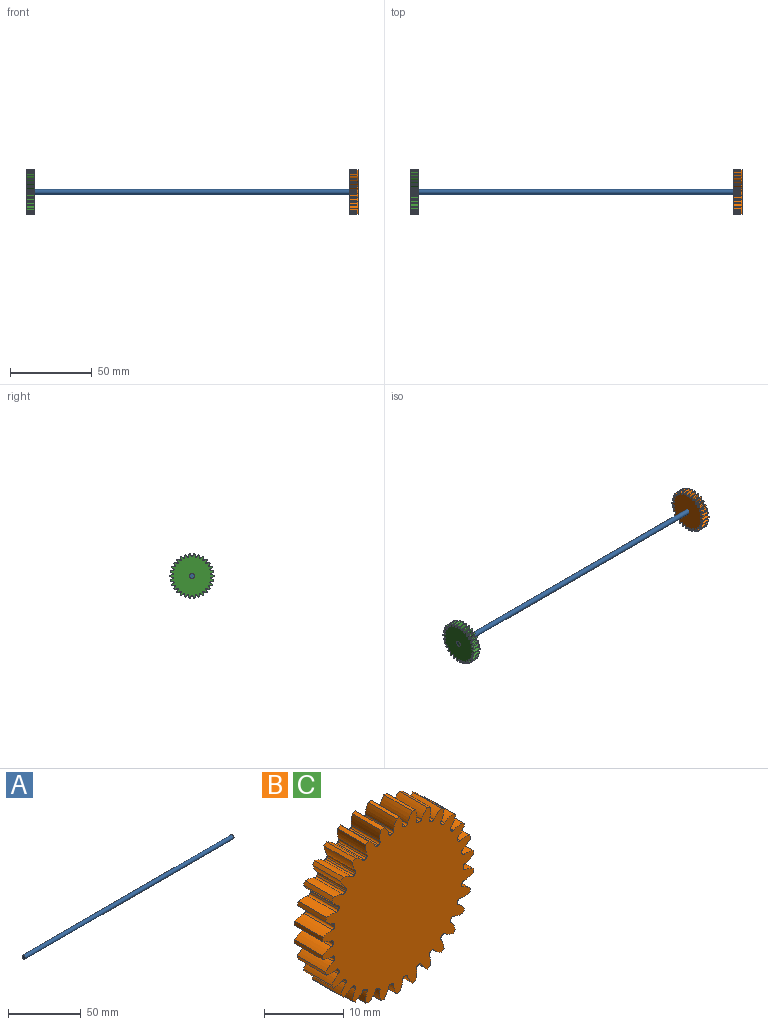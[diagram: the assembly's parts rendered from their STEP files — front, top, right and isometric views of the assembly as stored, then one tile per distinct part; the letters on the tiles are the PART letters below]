
ASSEMBLY  parts=3 mates=2
PART A: 3 faces, bbox 203.2x3.2x3.2 mm
  f0: cylinder r=1.59mm len=203.2mm, axis (-1,0,0), area 2026.8mm2, adj f1,f2
  f1: plane 3.18x3.18mm, normal (1,0,0), area 7.9mm2, adj f0
  f2: plane 3.18x3.18mm, normal (-1,0,0), area 7.9mm2, adj f0
PART B: 182 faces, bbox 27x5.1x27.1 mm
  f0: cylinder r=13.55mm len=5.08mm, axis (0,1,0), area 3.2mm2, adj f29,f31,f172,f179
  f1: cylinder r=13.55mm len=5.08mm, axis (0,1,0), area 3.2mm2, adj f29,f31,f167,f174
  f2: cylinder r=13.55mm len=5.08mm, axis (0,1,0), area 3.2mm2, adj f29,f31,f162,f169
  f3: cylinder r=13.55mm len=5.08mm, axis (0,1,0), area 3.2mm2, adj f29,f31,f152,f164
  f4: cylinder r=13.55mm len=5.08mm, axis (0,1,0), area 3.2mm2, adj f29,f31,f147,f159
  f5: cylinder r=13.55mm len=5.08mm, axis (0,1,0), area 3.2mm2, adj f29,f31,f154,f157
  f6: cylinder r=13.55mm len=5.08mm, axis (0,1,0), area 3.2mm2, adj f29,f31,f142,f149
  f7: cylinder r=13.55mm len=5.08mm, axis (0,1,0), area 3.2mm2, adj f29,f31,f32,f144
  f8: cylinder r=13.55mm len=5.08mm, axis (0,1,0), area 3.2mm2, adj f29,f31,f127,f139
  f9: cylinder r=13.55mm len=5.08mm, axis (0,1,0), area 3.2mm2, adj f29,f31,f134,f137
  f10: cylinder r=13.55mm len=5.08mm, axis (0,1,0), area 3.2mm2, adj f29,f31,f122,f129
  f11: cylinder r=13.55mm len=5.08mm, axis (0,1,0), area 3.2mm2, adj f29,f31,f124,f177
  f12: cylinder r=13.55mm len=5.08mm, axis (0,1,0), area 3.2mm2, adj f29,f31,f119,f132
  f13: cylinder r=13.55mm len=5.08mm, axis (0,1,0), area 3.2mm2, adj f29,f31,f114,f117
  f14: cylinder r=13.55mm len=5.08mm, axis (0,1,0), area 3.2mm2, adj f29,f31,f109,f112
  f15: cylinder r=13.55mm len=5.08mm, axis (0,1,0), area 3.2mm2, adj f29,f31,f104,f107
  f16: cylinder r=13.55mm len=5.08mm, axis (0,1,0), area 3.2mm2, adj f29,f31,f87,f99
  f17: cylinder r=13.55mm len=5.08mm, axis (0,1,0), area 3.2mm2, adj f29,f31,f94,f97
  f18: cylinder r=13.55mm len=5.08mm, axis (0,1,0), area 3.2mm2, adj f29,f31,f82,f89
  f19: cylinder r=13.55mm len=5.08mm, axis (0,1,0), area 3.2mm2, adj f29,f31,f84,f102
  f20: cylinder r=13.55mm len=5.08mm, axis (0,1,0), area 3.2mm2, adj f29,f31,f79,f92
  f21: cylinder r=13.55mm len=5.08mm, axis (0,1,0), area 3.2mm2, adj f29,f31,f74,f77
  f22: cylinder r=13.55mm len=5.08mm, axis (0,1,0), area 3.2mm2, adj f29,f31,f69,f72
  f23: cylinder r=13.55mm len=5.08mm, axis (0,1,0), area 3.2mm2, adj f29,f31,f64,f67
  f24: cylinder r=13.55mm len=5.08mm, axis (0,1,0), area 3.2mm2, adj f29,f31,f52,f59
  f25: cylinder r=13.55mm len=5.08mm, axis (0,1,0), area 3.2mm2, adj f29,f31,f42,f54
  f26: cylinder r=13.55mm len=5.08mm, axis (0,1,0), area 3.2mm2, adj f29,f31,f49,f62
  f27: cylinder r=13.55mm len=5.08mm, axis (0,1,0), area 3.2mm2, adj f29,f31,f44,f47
  f28: cylinder r=13.55mm len=5.08mm, axis (0,1,0), area 3.2mm2, adj f29,f31,f39,f57
  f29: plane 27.09x27.01mm, normal (0,-1,0), area 501mm2, adj f0,f1,f2,f3,f4,f5,f6,f7
  f30: cylinder r=13.55mm len=5.08mm, axis (0,1,0), area 3.2mm2, adj f29,f31,f34,f37
  f31: plane 27.09x27.01mm, normal (0,1,0), area 501mm2, adj f0,f1,f2,f3,f4,f5,f6,f7
  f32: extruded ~5.08x1.57mm, area 8.7mm2, adj f7,f29,f31,f35
  f33: cylinder r=11.64mm len=5.08mm, axis (0,1,0), area 1.4mm2, adj f29,f31,f35,f36
  f34: extruded ~5.08x1.57mm, area 8.7mm2, adj f29,f30,f31,f36
  f35: cylinder r=0.31mm len=5.08mm, axis (0,1,0), area 2.4mm2, adj f29,f31,f32,f33
  f36: cylinder r=0.31mm len=5.08mm, axis (0,1,0), area 2.4mm2, adj f29,f31,f33,f34
  f37: extruded ~5.08x1.67mm, area 8.7mm2, adj f29,f30,f31,f40
  f38: cylinder r=11.64mm len=5.08mm, axis (0,1,0), area 1.4mm2, adj f29,f31,f40,f41
  f39: extruded ~5.08x1.4mm, area 8.7mm2, adj f28,f29,f31,f41
  f40: cylinder r=0.31mm len=5.08mm, axis (0,1,0), area 2.4mm2, adj f29,f31,f37,f38
  f41: cylinder r=0.31mm len=5.08mm, axis (0,1,0), area 2.4mm2, adj f29,f31,f38,f39
  f42: extruded ~5.08x1.54mm, area 8.7mm2, adj f25,f29,f31,f45
  f43: cylinder r=11.64mm len=5.08mm, axis (0,1,0), area 1.4mm2, adj f29,f31,f45,f46
  f44: extruded ~5.08x1.61mm, area 8.7mm2, adj f27,f29,f31,f46
  f45: cylinder r=0.31mm len=5.08mm, axis (0,1,0), area 2.4mm2, adj f29,f31,f42,f43
  f46: cylinder r=0.31mm len=5.08mm, axis (0,1,0), area 2.4mm2, adj f29,f31,f43,f44
  f47: extruded ~5.08x1.36mm, area 8.7mm2, adj f27,f29,f31,f50
  f48: cylinder r=11.64mm len=5.08mm, axis (0,1,0), area 1.4mm2, adj f29,f31,f50,f51
  f49: extruded ~5.08x1.69mm, area 8.7mm2, adj f26,f29,f31,f51
  f50: cylinder r=0.31mm len=5.08mm, axis (0,1,0), area 2.4mm2, adj f29,f31,f47,f48
  f51: cylinder r=0.31mm len=5.08mm, axis (0,1,0), area 2.4mm2, adj f29,f31,f48,f49
  f52: extruded ~5.08x1.66mm, area 8.7mm2, adj f24,f29,f31,f55
  f53: cylinder r=11.64mm len=5.08mm, axis (0,1,0), area 1.4mm2, adj f29,f31,f55,f56
  f54: extruded ~5.08x1.46mm, area 8.7mm2, adj f25,f29,f31,f56
  f55: cylinder r=0.31mm len=5.08mm, axis (0,1,0), area 2.4mm2, adj f29,f31,f52,f53
  f56: cylinder r=0.31mm len=5.08mm, axis (0,1,0), area 2.4mm2, adj f29,f31,f53,f54
  f57: extruded ~5.08x1.7mm, area 8.7mm2, adj f28,f29,f31,f60
  f58: cylinder r=11.64mm len=5.08mm, axis (0,1,0), area 1.4mm2, adj f29,f31,f60,f61
  f59: extruded ~5.08x1.24mm, area 8.7mm2, adj f24,f29,f31,f61
  f60: cylinder r=0.31mm len=5.08mm, axis (0,1,0), area 2.4mm2, adj f29,f31,f57,f58
  f61: cylinder r=0.31mm len=5.08mm, axis (0,1,0), area 2.4mm2, adj f29,f31,f58,f59
  f62: extruded ~5.08x1.29mm, area 8.7mm2, adj f26,f29,f31,f65
  f63: cylinder r=11.64mm len=5.08mm, axis (0,1,0), area 1.4mm2, adj f29,f31,f65,f66
  f64: extruded ~5.08x1.7mm, area 8.7mm2, adj f23,f29,f31,f66
  f65: cylinder r=0.31mm len=5.08mm, axis (0,1,0), area 2.4mm2, adj f29,f31,f62,f63
  f66: cylinder r=0.31mm len=5.08mm, axis (0,1,0), area 2.4mm2, adj f29,f31,f63,f64
  f67: extruded ~5.08x1.49mm, area 8.7mm2, adj f23,f29,f31,f70
  f68: cylinder r=11.64mm len=5.08mm, axis (0,1,0), area 1.4mm2, adj f29,f31,f70,f71
  f69: extruded ~5.08x1.63mm, area 8.7mm2, adj f22,f29,f31,f71
  f70: cylinder r=0.31mm len=5.08mm, axis (0,1,0), area 2.4mm2, adj f29,f31,f67,f68
  f71: cylinder r=0.31mm len=5.08mm, axis (0,1,0), area 2.4mm2, adj f29,f31,f68,f69
  f72: extruded ~5.08x1.63mm, area 8.7mm2, adj f22,f29,f31,f75
  f73: cylinder r=11.64mm len=5.08mm, axis (0,1,0), area 1.4mm2, adj f29,f31,f75,f76
  f74: extruded ~5.08x1.49mm, area 8.7mm2, adj f21,f29,f31,f76
  f75: cylinder r=0.31mm len=5.08mm, axis (0,1,0), area 2.4mm2, adj f29,f31,f72,f73
  f76: cylinder r=0.31mm len=5.08mm, axis (0,1,0), area 2.4mm2, adj f29,f31,f73,f74
  f77: extruded ~5.08x1.7mm, area 8.7mm2, adj f21,f29,f31,f80
  f78: cylinder r=11.64mm len=5.08mm, axis (0,1,0), area 1.4mm2, adj f29,f31,f80,f81
  f79: extruded ~5.08x1.29mm, area 8.7mm2, adj f20,f29,f31,f81
  f80: cylinder r=0.31mm len=5.08mm, axis (0,1,0), area 2.4mm2, adj f29,f31,f77,f78
  f81: cylinder r=0.31mm len=5.08mm, axis (0,1,0), area 2.4mm2, adj f29,f31,f78,f79
  f82: extruded ~5.08x1.24mm, area 8.7mm2, adj f18,f29,f31,f85
  f83: cylinder r=11.64mm len=5.08mm, axis (0,1,0), area 1.4mm2, adj f29,f31,f85,f86
  f84: extruded ~5.08x1.7mm, area 8.7mm2, adj f19,f29,f31,f86
  f85: cylinder r=0.31mm len=5.08mm, axis (0,1,0), area 2.4mm2, adj f29,f31,f82,f83
  f86: cylinder r=0.31mm len=5.08mm, axis (0,1,0), area 2.4mm2, adj f29,f31,f83,f84
  f87: extruded ~5.08x1.46mm, area 8.7mm2, adj f16,f29,f31,f90
  f88: cylinder r=11.64mm len=5.08mm, axis (0,1,0), area 1.4mm2, adj f29,f31,f90,f91
  f89: extruded ~5.08x1.66mm, area 8.7mm2, adj f18,f29,f31,f91
  f90: cylinder r=0.31mm len=5.08mm, axis (0,1,0), area 2.4mm2, adj f29,f31,f87,f88
  f91: cylinder r=0.31mm len=5.08mm, axis (0,1,0), area 2.4mm2, adj f29,f31,f88,f89
  f92: extruded ~5.08x1.69mm, area 8.7mm2, adj f20,f29,f31,f95
  f93: cylinder r=11.64mm len=5.08mm, axis (0,1,0), area 1.4mm2, adj f29,f31,f95,f96
  f94: extruded ~5.08x1.36mm, area 8.7mm2, adj f17,f29,f31,f96
  f95: cylinder r=0.31mm len=5.08mm, axis (0,1,0), area 2.4mm2, adj f29,f31,f92,f93
  f96: cylinder r=0.31mm len=5.08mm, axis (0,1,0), area 2.4mm2, adj f29,f31,f93,f94
  f97: extruded ~5.08x1.61mm, area 8.7mm2, adj f17,f29,f31,f100
  f98: cylinder r=11.64mm len=5.08mm, axis (0,1,0), area 1.4mm2, adj f29,f31,f100,f101
  f99: extruded ~5.08x1.54mm, area 8.7mm2, adj f16,f29,f31,f101
  f100: cylinder r=0.31mm len=5.08mm, axis (0,1,0), area 2.4mm2, adj f29,f31,f97,f98
  f101: cylinder r=0.31mm len=5.08mm, axis (0,1,0), area 2.4mm2, adj f29,f31,f98,f99
  f102: extruded ~5.08x1.4mm, area 8.7mm2, adj f19,f29,f31,f105
  f103: cylinder r=11.64mm len=5.08mm, axis (0,1,0), area 1.4mm2, adj f29,f31,f105,f106
  f104: extruded ~5.08x1.67mm, area 8.7mm2, adj f15,f29,f31,f106
  f105: cylinder r=0.31mm len=5.08mm, axis (0,1,0), area 2.4mm2, adj f29,f31,f102,f103
  f106: cylinder r=0.31mm len=5.08mm, axis (0,1,0), area 2.4mm2, adj f29,f31,f103,f104
  f107: extruded ~5.08x1.57mm, area 8.7mm2, adj f15,f29,f31,f110
  f108: cylinder r=11.64mm len=5.08mm, axis (0,1,0), area 1.4mm2, adj f29,f31,f110,f111
  f109: extruded ~5.08x1.57mm, area 8.7mm2, adj f14,f29,f31,f111
  f110: cylinder r=0.31mm len=5.08mm, axis (0,1,0), area 2.4mm2, adj f29,f31,f107,f108
  f111: cylinder r=0.31mm len=5.08mm, axis (0,1,0), area 2.4mm2, adj f29,f31,f108,f109
  f112: extruded ~5.08x1.67mm, area 8.7mm2, adj f14,f29,f31,f115
  f113: cylinder r=11.64mm len=5.08mm, axis (0,1,0), area 1.4mm2, adj f29,f31,f115,f116
  f114: extruded ~5.08x1.4mm, area 8.7mm2, adj f13,f29,f31,f116
  f115: cylinder r=0.31mm len=5.08mm, axis (0,1,0), area 2.4mm2, adj f29,f31,f112,f113
  f116: cylinder r=0.31mm len=5.08mm, axis (0,1,0), area 2.4mm2, adj f29,f31,f113,f114
  f117: extruded ~5.08x1.7mm, area 8.7mm2, adj f13,f29,f31,f120
  f118: cylinder r=11.64mm len=5.08mm, axis (0,1,0), area 1.4mm2, adj f29,f31,f120,f121
  f119: extruded ~5.08x1.24mm, area 8.7mm2, adj f12,f29,f31,f121
  f120: cylinder r=0.31mm len=5.08mm, axis (0,1,0), area 2.4mm2, adj f29,f31,f117,f118
  f121: cylinder r=0.31mm len=5.08mm, axis (0,1,0), area 2.4mm2, adj f29,f31,f118,f119
  f122: extruded ~5.08x1.29mm, area 8.7mm2, adj f10,f29,f31,f125
  f123: cylinder r=11.64mm len=5.08mm, axis (0,1,0), area 1.4mm2, adj f29,f31,f125,f126
  f124: extruded ~5.08x1.7mm, area 8.7mm2, adj f11,f29,f31,f126
  f125: cylinder r=0.31mm len=5.08mm, axis (0,1,0), area 2.4mm2, adj f29,f31,f122,f123
  f126: cylinder r=0.31mm len=5.08mm, axis (0,1,0), area 2.4mm2, adj f29,f31,f123,f124
  f127: extruded ~5.08x1.36mm, area 8.7mm2, adj f8,f29,f31,f130
  f128: cylinder r=11.64mm len=5.08mm, axis (0,1,0), area 1.4mm2, adj f29,f31,f130,f131
  f129: extruded ~5.08x1.69mm, area 8.7mm2, adj f10,f29,f31,f131
  f130: cylinder r=0.31mm len=5.08mm, axis (0,1,0), area 2.4mm2, adj f29,f31,f127,f128
  f131: cylinder r=0.31mm len=5.08mm, axis (0,1,0), area 2.4mm2, adj f29,f31,f128,f129
  f132: extruded ~5.08x1.66mm, area 8.7mm2, adj f12,f29,f31,f135
  f133: cylinder r=11.64mm len=5.08mm, axis (0,1,0), area 1.4mm2, adj f29,f31,f135,f136
  f134: extruded ~5.08x1.46mm, area 8.7mm2, adj f9,f29,f31,f136
  f135: cylinder r=0.31mm len=5.08mm, axis (0,1,0), area 2.4mm2, adj f29,f31,f132,f133
  f136: cylinder r=0.31mm len=5.08mm, axis (0,1,0), area 2.4mm2, adj f29,f31,f133,f134
  f137: extruded ~5.08x1.54mm, area 8.7mm2, adj f9,f29,f31,f140
  f138: cylinder r=11.64mm len=5.08mm, axis (0,1,0), area 1.4mm2, adj f29,f31,f140,f141
  f139: extruded ~5.08x1.61mm, area 8.7mm2, adj f8,f29,f31,f141
  f140: cylinder r=0.31mm len=5.08mm, axis (0,1,0), area 2.4mm2, adj f29,f31,f137,f138
  f141: cylinder r=0.31mm len=5.08mm, axis (0,1,0), area 2.4mm2, adj f29,f31,f138,f139
  f142: extruded ~5.08x1.4mm, area 8.7mm2, adj f6,f29,f31,f145
  f143: cylinder r=11.64mm len=5.08mm, axis (0,1,0), area 1.4mm2, adj f29,f31,f145,f146
  f144: extruded ~5.08x1.67mm, area 8.7mm2, adj f7,f29,f31,f146
  f145: cylinder r=0.31mm len=5.08mm, axis (0,1,0), area 2.4mm2, adj f29,f31,f142,f143
  f146: cylinder r=0.31mm len=5.08mm, axis (0,1,0), area 2.4mm2, adj f29,f31,f143,f144
  f147: extruded ~5.08x1.24mm, area 8.7mm2, adj f4,f29,f31,f150
  f148: cylinder r=11.64mm len=5.08mm, axis (0,1,0), area 1.4mm2, adj f29,f31,f150,f151
  f149: extruded ~5.08x1.7mm, area 8.7mm2, adj f6,f29,f31,f151
  f150: cylinder r=0.31mm len=5.08mm, axis (0,1,0), area 2.4mm2, adj f29,f31,f147,f148
  f151: cylinder r=0.31mm len=5.08mm, axis (0,1,0), area 2.4mm2, adj f29,f31,f148,f149
  f152: extruded ~5.08x1.61mm, area 8.7mm2, adj f3,f29,f31,f155
  f153: cylinder r=11.64mm len=5.08mm, axis (0,1,0), area 1.4mm2, adj f29,f31,f155,f156
  f154: extruded ~5.08x1.54mm, area 8.7mm2, adj f5,f29,f31,f156
  f155: cylinder r=0.31mm len=5.08mm, axis (0,1,0), area 2.4mm2, adj f29,f31,f152,f153
  f156: cylinder r=0.31mm len=5.08mm, axis (0,1,0), area 2.4mm2, adj f29,f31,f153,f154
  f157: extruded ~5.08x1.46mm, area 8.7mm2, adj f5,f29,f31,f160
  f158: cylinder r=11.64mm len=5.08mm, axis (0,1,0), area 1.4mm2, adj f29,f31,f160,f161
  f159: extruded ~5.08x1.66mm, area 8.7mm2, adj f4,f29,f31,f161
  f160: cylinder r=0.31mm len=5.08mm, axis (0,1,0), area 2.4mm2, adj f29,f31,f157,f158
  f161: cylinder r=0.31mm len=5.08mm, axis (0,1,0), area 2.4mm2, adj f29,f31,f158,f159
  f162: extruded ~5.08x1.69mm, area 8.7mm2, adj f2,f29,f31,f165
  f163: cylinder r=11.64mm len=5.08mm, axis (0,1,0), area 1.4mm2, adj f29,f31,f165,f166
  f164: extruded ~5.08x1.36mm, area 8.7mm2, adj f3,f29,f31,f166
  f165: cylinder r=0.31mm len=5.08mm, axis (0,1,0), area 2.4mm2, adj f29,f31,f162,f163
  f166: cylinder r=0.31mm len=5.08mm, axis (0,1,0), area 2.4mm2, adj f29,f31,f163,f164
  f167: extruded ~5.08x1.7mm, area 8.7mm2, adj f1,f29,f31,f170
  f168: cylinder r=11.64mm len=5.08mm, axis (0,1,0), area 1.4mm2, adj f29,f31,f170,f171
  f169: extruded ~5.08x1.29mm, area 8.7mm2, adj f2,f29,f31,f171
  f170: cylinder r=0.31mm len=5.08mm, axis (0,1,0), area 2.4mm2, adj f29,f31,f167,f168
  f171: cylinder r=0.31mm len=5.08mm, axis (0,1,0), area 2.4mm2, adj f29,f31,f168,f169
  f172: extruded ~5.08x1.63mm, area 8.7mm2, adj f0,f29,f31,f175
  f173: cylinder r=11.64mm len=5.08mm, axis (0,1,0), area 1.4mm2, adj f29,f31,f175,f176
  f174: extruded ~5.08x1.49mm, area 8.7mm2, adj f1,f29,f31,f176
  f175: cylinder r=0.31mm len=5.08mm, axis (0,1,0), area 2.4mm2, adj f29,f31,f172,f173
  f176: cylinder r=0.31mm len=5.08mm, axis (0,1,0), area 2.4mm2, adj f29,f31,f173,f174
  f177: extruded ~5.08x1.49mm, area 8.7mm2, adj f11,f29,f31,f180
  f178: cylinder r=11.64mm len=5.08mm, axis (0,1,0), area 1.4mm2, adj f29,f31,f180,f181
  f179: extruded ~5.08x1.63mm, area 8.7mm2, adj f0,f29,f31,f181
  f180: cylinder r=0.31mm len=5.08mm, axis (0,1,0), area 2.4mm2, adj f29,f31,f177,f178
  f181: cylinder r=0.31mm len=5.08mm, axis (0,1,0), area 2.4mm2, adj f29,f31,f178,f179
PART C: same geometry as B
PLACE A t=(-108.58,-47.04,-45.13)mm
PLACE B rot(axis=(-0.58,0.58,0.58),120deg) t=(89.54,-9.26,-7.85)mm
PLACE C rot(axis=(-0.58,-0.58,-0.58),120deg) t=(-103.5,-9.26,-7.85)mm
MATE fastened B.f0 <-> A.f0  axis (1,0,0) through (94.62,-9.26,-7.85)mm
MATE fastened C.f0 <-> A.f0  axis (-1,0,0) through (-108.58,-9.26,-7.85)mm
